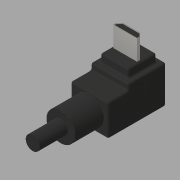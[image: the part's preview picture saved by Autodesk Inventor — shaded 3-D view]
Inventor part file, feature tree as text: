
AUTODESK INVENTOR PART (.ipt)
format: ipt  version: 2019 (Build 230136000, 136)  size: 231,936 bytes
history: native  units: mm
features: extrude x7, sketch x7, projected_geometry x4, other x2, fillet x1
ambient origin geometry x8: Origin, YZ Plane, XZ Plane, XY Plane, X Axis, Y Axis, Z Axis, Center Point
bodies: Solid1 (feature_tree), Solid2 (feature_tree)
feature tree (21):
  extrude  "Extrusion1"  Depth=16.5mm
  extrude  "Extrusion2"  Depth=10.75mm
  extrude  "Extrusion3"  TaperAngle=0.0deg  [1 undecoded]
  fillet  "Fillet1"  Radius=8.0mm
  extrude  "Extrusion4"  Depth=2.33mm TaperAngle=0.0deg
  extrude  "Extrusion5"  Depth=8.15mm
  extrude  "Extrusion6"  Depth=6.8mm
  extrude  "Extrusion7"  Depth=8.0mm
  other  "Work Axis1"
  sketch  "Sketch1"  dims[d0=10.75mm d1=16.5mm]
  sketch  "Sketch2"  dims[d2=9.0mm d3=0.0mm d4=10.75mm]
  sketch  "Sketch3"  dims[d5=1.75mm d6=0.0mm d7=8.0mm]
  projected_geometry  "Projected Loop1"
  sketch  "Sketch4"  dims[d8=8.0mm d9=2.33mm d10=0.0mm]
  projected_geometry  "Projected Loop2"
  sketch  "Sketch5"  dims[d11=0.5mm d12=8.15mm]
  projected_geometry  "Projected Loop3"
  sketch  "Sketch6"  dims[d13=8.15mm d14=0.0mm d15=6.8mm]
  projected_geometry  "Projected Loop4"
  sketch  "Sketch7"  dims[d16=1.85mm d17=0.85mm d18=1.0mm d19=1.0mm d20=0.85mm d21=5.75mm d22=0.0mm d23=0.15mm d24=0.15mm d25=0.0mm d26=4.0mm d27=8.0mm d28=0.0mm]
  other  "Work Point1"
note: 1 required parameter value undecoded (feature->parameter linkage not recoverable at this tier; creation-order binding heuristic only, values carry confidence <= 0.55)
